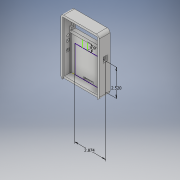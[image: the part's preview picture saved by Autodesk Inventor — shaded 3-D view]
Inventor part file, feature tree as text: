
AUTODESK INVENTOR PART (.ipt)
format: ipt  version: 2018 (Build 220112000, 112)  size: 373,248 bytes
history: native  units: in
note: dims shown in document units (in); Inventor stores cm internally (conversion verified against a paired STEP export)
features: sketch x15, extrude x13, projected_geometry x3
ambient origin geometry x8: Origin, YZ Plane, XZ Plane, XY Plane, X Axis, Y Axis, Z Axis, Center Point
bodies: Solid1 (feature_tree)
feature tree (31):
  extrude  "Extrusion1"  Depth=3.0709in
  extrude  "Extrusion2"  Depth=3.189in
  extrude  "Extrusion3"  Depth=1.0236in
  extrude  "Extrusion4"  Depth=0.2756in
  extrude  "Extrusion5"  Depth=0.2362in
  extrude  "Extrusion7"  Depth=0.1181in
  sketch  "Sketch8"  dims[d17=0.1063in d18=0.2559in d19=0.0in]
  extrude  "Extrusion8"  Depth=0.2559in TaperAngle=0.0deg
  extrude  "Extrusion9"  Depth=0.1969in
  sketch  "Sketch11"  dims[d24=0.2756in d25=0.3346in d26=0.0in]
  extrude  "Extrusion10"  Depth=0.1969in
  extrude  "Extrusion11"  Depth=0.3346in TaperAngle=0.0deg
  extrude  "Extrusion12"  Depth=0.1575in TaperAngle=0.0deg
  extrude  "Extrusion13"  Depth=1.6535in
  extrude  "Extrusion14"  Depth=0.1969in
  sketch  "Sketch1"  dims[d0=2.7953in d1=3.0709in]
  sketch  "Sketch2"  dims[d2=1.4567in d3=3.189in]
  sketch  "Sketch3"  dims[d4=2.8346in d5=1.0236in]
  sketch  "Sketch4"  dims[d6=0.185in d7=0.2756in]
  sketch  "Sketch5"  dims[d9=0.0197in d14=0.2362in]
  sketch  "Sketch7"  dims[d15=0.1181in d16=0.1063in]
  projected_geometry  "Projected Loop1"
  sketch  "Sketch9"  dims[d20=0.1969in d21=0.1969in]
  sketch  "Sketch10"  dims[d22=0.1969in d23=0.1969in]
  sketch  "Sketch12"  dims[d27=0.3346in d28=0.0in d35=0.1575in d36=0.0in]
  sketch  "Sketch13"  dims[d37=0.0394in d38=1.6535in]
  sketch  "Sketch14"  dims[d39=0.1181in d40=0.0in d41=0.1969in]
  sketch  "Sketch15"  dims[d42=0.1969in]
  projected_geometry  "Projected Loop2"
  sketch  "Sketch16"  dims[d43=0.2756in d44=0.0in d51=0.0299in d52=0.03in d53=0.6693in d54=0.0in d55=2.874in d56=2.5197in d57=0.7087in d58=0.1575in d59=0.0787in d60=0.0787in d61=0.6693in d62=0.0in d63=0.2283in d64=0.2362in d65=0.2362in d67=0.315in d68=1.0in d69=0.0in d70=2.5in d71=0.2362in d72=0.3346in d73=2.8919in d74=0.1673in d75=1.0in d76=0.0in d77=0.1181in d78=0.0in d79=0.2559in d80=0.2559in d81=0.128in d82=0.1181in d83=0.0in d84=0.1181in d85=0.0in d86=0.02in d87=0.0in]
  projected_geometry  "Projected Loop3"
